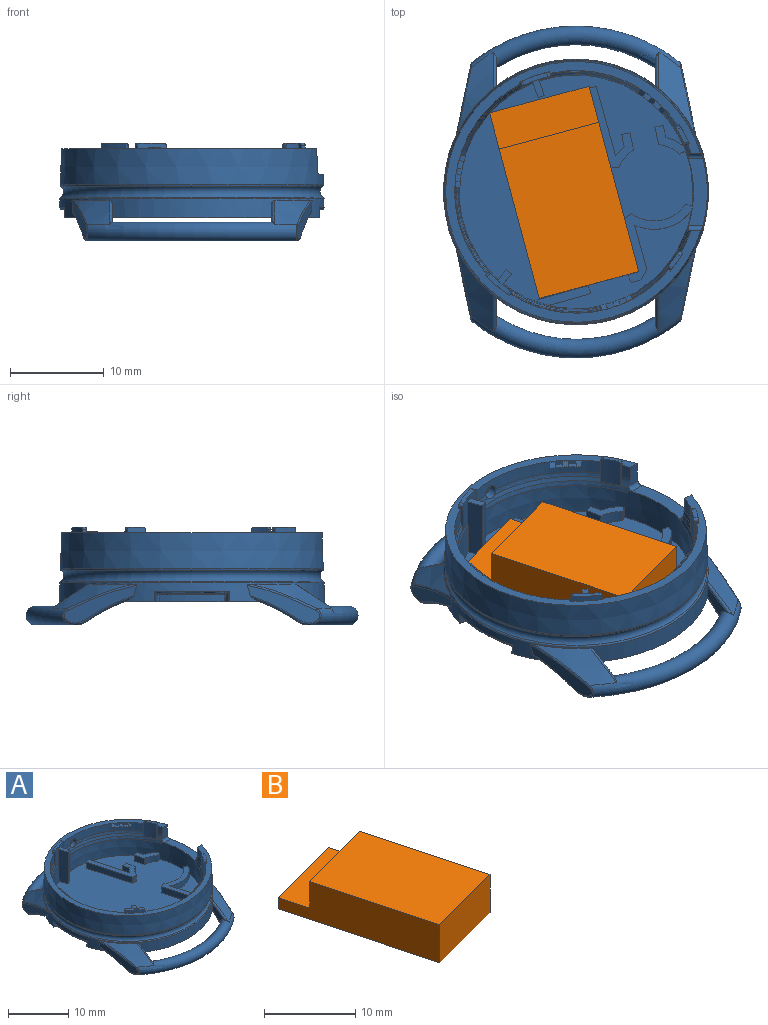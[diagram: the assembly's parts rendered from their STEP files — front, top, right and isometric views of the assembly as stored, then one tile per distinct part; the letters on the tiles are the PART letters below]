
ASSEMBLY  parts=2 mates=1
PART A: 217 faces, bbox 31.1x38.4x10.5 mm
  f0: plane 3.07x2.92mm, normal (-1,0,0), area 3.4mm2, adj f1,f17,f18,f28
  f1: cone r=14.15mm half-angle=2deg, axis (0,0,-1), area 109.4mm2, adj f0,f2,f4,f11,f12,f13,f15,f16
  f2: torus R=13.89mm, axis (0,0,-1), area 3.2mm2, adj f1,f3,f7,f10,f11,f216
  f3: plane 0.91x0.85mm, normal (0.28,0.96,0), area 0.7mm2, adj f2,f4,f6,f7,f216
  f4: plane 28.4x27.26mm, normal (0,0,-1), area 613.3mm2, adj f1,f3,f5,f6,f9,f10,f11,f12
  f5: cone r=13.08mm half-angle=5.2deg, axis (0,0,1), area 5mm2, adj f4,f6,f8,f9
  f6: cylinder r=0.15mm len=0.88mm, axis (0.09,-0.02,1), area 0.2mm2, adj f3,f4,f5,f7,f8
  f7: plane 7.66x1.15mm, normal (0,0,-1), area 4.8mm2, adj f2,f3,f6,f8,f9,f10
  f8: torus R=13.26mm, axis (0,0,-1), area 1.6mm2, adj f5,f6,f7,f9
  f9: cylinder r=0.15mm len=0.88mm, axis (-0.09,-0.02,-1), area 0.2mm2, adj f4,f5,f7,f8,f10
  f10: plane 0.91x0.85mm, normal (0.28,-0.96,0), area 0.7mm2, adj f2,f4,f7,f9,f11
  f11: cylinder r=0.1mm len=1.11mm, axis (-0.03,-0.01,1), area 0.2mm2, adj f1,f2,f4,f10
  f12: bspline ~5.59x2.9mm, area 3mm2, adj f1,f4,f13,f14,f29
  f13: plane 7.77x4.01mm, normal (0.98,0.19,-0.03), area 11mm2, adj f1,f12,f14,f15
  f14: bspline ~2.51x1.82mm, area 1.2mm2, adj f12,f13,f15,f18
  f15: bspline ~7.51x2.94mm, area 2mm2, adj f1,f13,f14,f16
  f16: cone r=15.73mm half-angle=51.5deg, axis (0,0,-1), area 19.2mm2, adj f1,f15,f17,f18
  f17: bspline ~4.16x2.88mm, area 2mm2, adj f0,f1,f16,f18
  f18: torus R=16.72mm, axis (0,0,1), area 134.1mm2, adj f0,f14,f16,f17,f19,f20,f21,f22
  f19: cone r=15.04mm half-angle=40.5deg, axis (0,0,-1), area 12.1mm2, adj f4,f18,f20,f24
  f20: bspline ~2.47x2.39mm, area 0.8mm2, adj f1,f4,f18,f19,f21
  f21: plane 3.07x2.92mm, normal (1,0,0), area 3.4mm2, adj f1,f18,f20,f22
  f22: bspline ~4.16x2.88mm, area 2mm2, adj f1,f18,f21,f27
  f23: bspline ~2.51x1.82mm, area 1.2mm2, adj f18,f24,f25,f26
  f24: bspline ~5.59x2.9mm, area 3mm2, adj f1,f4,f19,f23,f25
  f25: plane 7.76x4mm, normal (-0.98,0.19,-0.03), area 11mm2, adj f1,f23,f24,f26
  f26: bspline ~7.51x2.94mm, area 2mm2, adj f1,f23,f25,f27
  f27: cone r=15.73mm half-angle=51.5deg, axis (0,0,-1), area 19.2mm2, adj f1,f18,f22,f26
  f28: bspline ~2.47x2.39mm, area 0.8mm2, adj f0,f1,f4,f18,f29
  f29: cone r=15.04mm half-angle=40.5deg, axis (0,0,-1), area 12.1mm2, adj f4,f12,f18,f28
  f30: cylinder r=0.1mm len=1.11mm, axis (-0.03,0.01,-1), area 0.2mm2, adj f1,f4,f31,f32
  f31: torus R=13.89mm, axis (0,0,-1), area 3.2mm2, adj f1,f30,f32,f33,f38,f39
  f32: plane 0.91x0.85mm, normal (-0.28,-0.96,0), area 0.7mm2, adj f4,f30,f31,f33,f35
  f33: plane 7.66x1.15mm, normal (0,0,-1), area 4.8mm2, adj f31,f32,f34,f35,f37,f38
  f34: torus R=13.26mm, axis (0,0,-1), area 1.6mm2, adj f33,f35,f36,f37
  f35: cylinder r=0.15mm len=0.88mm, axis (0.09,-0.02,-1), area 0.2mm2, adj f4,f32,f33,f34,f36
  f36: cone r=13.08mm half-angle=5.2deg, axis (0,0,1), area 5mm2, adj f4,f34,f35,f37
  f37: cylinder r=0.15mm len=0.88mm, axis (-0.09,-0.02,1), area 0.2mm2, adj f4,f33,f34,f36,f38
  f38: plane 0.91x0.85mm, normal (-0.28,0.96,0), area 0.7mm2, adj f4,f31,f33,f37,f39
  f39: cylinder r=0.1mm len=1.11mm, axis (0.03,0.01,1), area 0.2mm2, adj f1,f4,f31,f38
  f40: bspline ~5.59x2.9mm, area 3mm2, adj f1,f4,f41,f46,f58
  f41: cone r=15.04mm half-angle=40.5deg, axis (0,0,-1), area 12.1mm2, adj f4,f40,f42,f45
  f42: bspline ~2.47x2.39mm, area 0.8mm2, adj f1,f4,f41,f43,f45
  f43: plane 3.07x2.92mm, normal (-1,0,0), area 3.4mm2, adj f1,f42,f44,f45
  f44: bspline ~4.16x2.88mm, area 2mm2, adj f1,f43,f45,f57
  f45: torus R=16.72mm, axis (0,0,1), area 134.1mm2, adj f41,f42,f43,f44,f46,f47,f51,f52
  f46: bspline ~2.51x1.82mm, area 1.2mm2, adj f40,f45,f56,f58
  f47: bspline ~2.51x1.82mm, area 1.2mm2, adj f45,f48,f49,f50
  f48: bspline ~5.59x2.9mm, area 3mm2, adj f1,f4,f47,f49,f55
  f49: plane 7.76x4mm, normal (-0.98,-0.19,-0.03), area 11mm2, adj f1,f47,f48,f50
  f50: bspline ~7.51x2.94mm, area 2mm2, adj f1,f47,f49,f51
  f51: cone r=15.73mm half-angle=51.5deg, axis (0,0,-1), area 19.2mm2, adj f1,f45,f50,f52
  f52: bspline ~4.16x2.88mm, area 2mm2, adj f1,f45,f51,f53
  f53: plane 3.07x2.92mm, normal (1,0,0), area 3.4mm2, adj f1,f45,f52,f54
  f54: bspline ~2.47x2.39mm, area 0.8mm2, adj f1,f4,f45,f53,f55
  f55: cone r=15.04mm half-angle=40.5deg, axis (0,0,-1), area 12.1mm2, adj f4,f45,f48,f54
  f56: bspline ~7.51x2.94mm, area 2mm2, adj f1,f46,f57,f58
  f57: cone r=15.73mm half-angle=51.5deg, axis (0,0,-1), area 19.2mm2, adj f1,f44,f45,f56
  f58: plane 7.77x4.01mm, normal (0.98,-0.19,-0.03), area 11mm2, adj f1,f40,f46,f56
  f59: torus R=13.86mm, axis (0,0,-1), area 21.4mm2, adj f1,f60
  f60: torus R=14.36mm, axis (0,0,-1), area 113.2mm2, adj f59,f61
  f61: torus R=13.81mm, axis (0,0,1), area 21.3mm2, adj f60,f62
  f62: cone r=13.99mm half-angle=2deg, axis (0,0,-1), area 312.4mm2, adj f61,f63,f94,f120,f121,f122,f177,f185
  f63: bspline ~1.82x1.79mm, area 1mm2, adj f62,f64,f177
  f64: cylinder r=0.75mm len=1.5mm, axis (0,1,0), area 4mm2, adj f63,f65,f69,f97,f124,f177
  f65: cone r=12.72mm half-angle=17.9deg, axis (0,0,1), area 7.6mm2, adj f64,f69,f71,f89,f97,f176
  f66: cone r=12.72mm half-angle=17.9deg, axis (0,0,1), area 11.7mm2, adj f87,f95,f96,f100,f104,f214
  f67: cone r=12.72mm half-angle=17.9deg, axis (0,0,1), area 10.5mm2, adj f88,f98,f99,f104,f105,f121,f122,f178
  f68: cone r=12.72mm half-angle=17.9deg, axis (0,0,1), area 0.5mm2, adj f70,f89,f93,f185,f186
  f69: torus R=10.9mm, axis (0,0,1), area 6.5mm2, adj f64,f65,f71,f124
  f70: torus R=10.9mm, axis (0,0,1), area 0.5mm2, adj f68,f93,f127,f185
  f71: plane 2.91x0.48mm, normal (-0.54,0.84,0.02), area 0.8mm2, adj f65,f69,f72,f73,f75,f90,f94,f124
  f72: cylinder r=0.3mm len=0.57mm, axis (-0.84,-0.54,0), area 0.2mm2, adj f71,f73,f75,f79
  f73: cone r=12.63mm half-angle=1deg, axis (0,0,1), area 7.1mm2, adj f71,f72,f74,f79,f90,f93
  f74: cylinder r=0.3mm len=0.56mm, axis (0.92,0.39,0), area 0.2mm2, adj f73,f75,f79,f93
  f75: cone r=13.14mm half-angle=2deg, axis (0,0,-1), area 1.3mm2, adj f71,f72,f74,f79,f93,f94
  f76: plane 2.75x1.38mm, normal (0,0,1), area 1.3mm2, adj f80,f81,f82,f83
  f77: plane 2.42x2.14mm, normal (0,0,1), area 1.3mm2, adj f101,f102,f103,f104
  f78: plane 1.62x1.33mm, normal (0,0,1), area 0.8mm2, adj f179,f180,f181,f182
  f79: plane 1.67x1.18mm, normal (0,0,1), area 0.8mm2, adj f72,f73,f74,f75
  f80: cylinder r=0.3mm len=0.54mm, axis (-0.22,0.98,0), area 0.2mm2, adj f76,f81,f83,f176
  f81: cone r=13.14mm half-angle=2deg, axis (0,0,-1), area 2mm2, adj f76,f80,f82,f94,f95,f176
  f82: cylinder r=0.3mm len=0.57mm, axis (0.46,-0.89,0), area 0.2mm2, adj f76,f81,f83,f95
  f83: cone r=12.63mm half-angle=1deg, axis (0,0,1), area 8.7mm2, adj f76,f80,f82,f84,f86,f91,f92,f95
  f84: plane 1.94x1.28mm, normal (0,0,1), area 1.3mm2, adj f83,f86,f212,f213
  f85: plane 1.59x1.5mm, normal (0,0,1), area 1mm2, adj f104,f105,f214,f215
  f86: plane 6.5x1.72mm, normal (0.94,0.34,0), area 11.2mm2, adj f83,f84,f89,f106,f117,f213
  f87: torus R=14.55mm, axis (0,0,1), area 15.2mm2, adj f66,f92,f118,f212,f214
  f88: torus R=14.55mm, axis (0,0,1), area 14.3mm2, adj f67,f105,f117,f120,f121,f187
  f89: torus R=14.55mm, axis (0,0,1), area 11.7mm2, adj f65,f68,f86,f90,f91,f117,f119,f120
  f90: cone r=12.62mm half-angle=17.9deg, axis (0,0,1), area 0.3mm2, adj f71,f73,f89,f93
  f91: cone r=12.62mm half-angle=17.9deg, axis (0,0,1), area 0.2mm2, adj f83,f89,f176
  f92: cone r=12.62mm half-angle=17.9deg, axis (0,0,1), area 0.2mm2, adj f83,f87,f95
  f93: plane 2.91x0.48mm, normal (0.39,-0.92,0.02), area 0.8mm2, adj f68,f70,f73,f74,f75,f90,f94,f127
  f94: plane 27.85x27.24mm, normal (0,0,1), area 71.4mm2, adj f62,f71,f75,f81,f93,f95,f100,f102
  f95: plane 2.91x0.51mm, normal (-0.89,-0.46,0.02), area 0.8mm2, adj f66,f81,f82,f83,f92,f94,f96,f123
  f96: torus R=10.9mm, axis (0,0,1), area 12.7mm2, adj f66,f95,f100,f123
  f97: torus R=10.9mm, axis (0,0,1), area 1.2mm2, adj f64,f65,f124,f176
  f98: torus R=10.9mm, axis (0,0,1), area 10mm2, adj f67,f126,f183,f184
  f99: torus R=10.9mm, axis (0,0,1), area 1.4mm2, adj f67,f122,f125,f178
  f100: plane 2.77x0.37mm, normal (-0.68,0.74,0.02), area 0.7mm2, adj f66,f94,f96,f101,f102,f104,f123
  f101: cylinder r=0.3mm len=0.57mm, axis (-0.74,-0.68,0), area 0.2mm2, adj f77,f100,f102,f104
  f102: cone r=13.14mm half-angle=2deg, axis (0,0,-1), area 2mm2, adj f77,f94,f100,f101,f103,f184
  f103: cylinder r=0.3mm len=0.58mm, axis (0.54,0.84,0), area 0.2mm2, adj f77,f102,f104,f184
  f104: cylinder r=12.65mm len=3.07mm, axis (0,0,1), area 8.3mm2, adj f66,f67,f77,f85,f100,f101,f103,f105
  f105: plane 6.49x1.15mm, normal (0.77,-0.64,0), area 9.2mm2, adj f67,f85,f88,f104,f106,f117,f215
  f106: plane 24.98x24.98mm, normal (0,0,1), area 455.3mm2, adj f86,f105,f107,f108,f109,f110,f111,f112
  f107: plane 1.25x0.95mm, normal (-0.05,-1,0), area 1.2mm2, adj f106,f108,f115,f116
  f108: plane 8.38x2.32mm, normal (-0.96,-0.27,0), area 10.9mm2, adj f106,f107,f109,f116
  f109: plane 1.25x0.87mm, normal (-0.27,0.96,0), area 1.1mm2, adj f106,f108,f110,f116
  f110: plane 7.44x2.05mm, normal (0.96,0.27,0), area 9.6mm2, adj f106,f109,f111,f116
  f111: cylinder r=5mm len=1.25mm, axis (0,0,1), area 1.7mm2, adj f106,f110,f112,f116
  f112: plane 1.27x1.25mm, normal (-0.98,-0.22,0), area 1.6mm2, adj f106,f111,f113,f116
  f113: plane 1.25x0.88mm, normal (-0.22,0.98,0), area 1.1mm2, adj f106,f112,f114,f116
  f114: plane 1.84x1.25mm, normal (0.98,0.22,0), area 2.4mm2, adj f106,f113,f115,f116
  f115: cylinder r=4.1mm len=1.85mm, axis (0,0,1), area 3.1mm2, adj f106,f107,f114,f116
  f116: plane 8.67x4.85mm, normal (0,0,1), area 11.1mm2, adj f107,f108,f109,f110,f111,f112,f113,f114
  f117: cone r=12.52mm half-angle=1deg, axis (0,0,1), area 171mm2, adj f86,f88,f89,f105,f106,f119,f120,f187
  f118: cone r=12.52mm half-angle=1deg, axis (0,0,1), area 83.7mm2, adj f87,f106,f212,f214
  f119: plane 0.32x0.04mm, normal (0,1,0), area 0mm2, adj f89,f117,f120
  f120: plane 8.15x2.15mm, normal (0,0,1), area 10.7mm2, adj f62,f88,f89,f117,f119,f121,f186,f187
  f121: cylinder r=0.5mm len=1.57mm, axis (1,0,0), area 1.1mm2, adj f62,f67,f88,f120,f122
  f122: plane 2.26x1.36mm, normal (0,1,0), area 2.5mm2, adj f62,f67,f94,f99,f121,f125
  f123: cone r=12.93mm half-angle=2.5deg, axis (0,0,1), area 31.8mm2, adj f94,f95,f96,f100,f128,f129,f130,f132
  f124: cone r=12.93mm half-angle=2.5deg, axis (0,0,1), area 19.1mm2, adj f64,f69,f71,f94,f97,f160,f161,f162
  f125: cone r=12.93mm half-angle=2.5deg, axis (0,0,1), area 3.9mm2, adj f94,f99,f122,f178
  f126: cone r=12.93mm half-angle=2.5deg, axis (0,0,1), area 24.3mm2, adj f94,f98,f144,f145,f146,f148,f149,f150
  f127: cone r=12.93mm half-angle=2.5deg, axis (0,0,1), area 1.5mm2, adj f70,f93,f94,f185
  f128: plane 0.59x0.22mm, normal (0,0,1), area 0mm2, adj f123,f131,f132,f139
  f129: plane 0.6x0.16mm, normal (0,0,1), area 0mm2, adj f123,f141,f142,f143
  f130: plane 0.61x0.09mm, normal (0,0,1), area 0mm2, adj f123,f134,f135,f136
  f131: cone r=12.65mm half-angle=51.3deg, axis (0,0,1), area 0.4mm2, adj f128,f132,f139,f140
  f132: plane 1.1x0.55mm, normal (0.17,0.98,0), area 0.5mm2, adj f123,f128,f131,f133,f140
  f133: plane 3.46x1.1mm, normal (0,0,-1), area 1.7mm2, adj f123,f132,f134,f140
  f134: plane 1.1x0.55mm, normal (-0.17,-0.98,0), area 0.5mm2, adj f123,f130,f133,f135,f140
  f135: cone r=12.65mm half-angle=51.3deg, axis (0,0,1), area 0.4mm2, adj f130,f134,f136,f140
  f136: plane 0.55x0.4mm, normal (0.17,0.98,0), area 0.1mm2, adj f123,f130,f135,f138
  f137: plane 0.91x0.72mm, normal (0,0,1), area 0.5mm2, adj f123,f139,f140,f142
  f138: plane 0.88x0.62mm, normal (0,0,1), area 0.4mm2, adj f123,f136,f140,f143
  f139: plane 0.55x0.4mm, normal (-0.17,-0.98,0), area 0.1mm2, adj f123,f128,f131,f137
  f140: cylinder r=12.4mm len=3.38mm, axis (0,0,-1), area 2.4mm2, adj f131,f132,f133,f134,f135,f137,f138,f141
  f141: cone r=12.65mm half-angle=51.3deg, axis (0,0,1), area 0.4mm2, adj f129,f140,f142,f143
  f142: plane 0.55x0.4mm, normal (0.17,0.98,0), area 0.1mm2, adj f123,f129,f137,f141
  f143: plane 0.55x0.4mm, normal (-0.17,-0.98,0), area 0.1mm2, adj f123,f129,f138,f141
  f144: plane 0.61x0.19mm, normal (0,0,1), area 0mm2, adj f126,f147,f148,f155
  f145: plane 0.58x0.26mm, normal (0,0,1), area 0mm2, adj f126,f157,f158,f159
  f146: plane 0.56x0.32mm, normal (0,0,1), area 0mm2, adj f126,f150,f151,f152
  f147: cone r=12.65mm half-angle=51.3deg, axis (0,0,1), area 0.4mm2, adj f144,f148,f155,f156
  f148: plane 1.1x0.53mm, normal (-0.94,-0.34,0), area 0.5mm2, adj f126,f144,f147,f149,f156
  f149: plane 3.4x1.65mm, normal (0,0,-1), area 1.7mm2, adj f126,f148,f150,f156
  f150: plane 1.1x0.53mm, normal (0.94,0.34,0), area 0.5mm2, adj f126,f146,f149,f151,f156
  f151: cone r=12.65mm half-angle=51.3deg, axis (0,0,1), area 0.4mm2, adj f146,f150,f152,f156
  f152: plane 0.52x0.4mm, normal (-0.94,-0.34,0), area 0.1mm2, adj f126,f146,f151,f154
  f153: plane 0.99x0.75mm, normal (0,0,1), area 0.5mm2, adj f126,f155,f156,f158
  f154: plane 0.91x0.82mm, normal (0,0,1), area 0.4mm2, adj f126,f152,f156,f159
  f155: plane 0.52x0.4mm, normal (0.94,0.34,0), area 0.1mm2, adj f126,f144,f147,f153
  f156: cylinder r=12.4mm len=3.22mm, axis (0,0,-1), area 2.4mm2, adj f147,f148,f149,f150,f151,f153,f154,f157
  f157: cone r=12.65mm half-angle=51.3deg, axis (0,0,1), area 0.4mm2, adj f145,f156,f158,f159
  f158: plane 0.52x0.4mm, normal (-0.94,-0.34,0), area 0.1mm2, adj f126,f145,f153,f157
  f159: plane 0.52x0.4mm, normal (0.94,0.34,0), area 0.1mm2, adj f126,f145,f154,f157
  f160: plane 0.48x0.45mm, normal (0,0,1), area 0mm2, adj f124,f163,f164,f171
  f161: plane 0.5x0.43mm, normal (0,0,1), area 0mm2, adj f124,f173,f174,f175
  f162: plane 0.54x0.38mm, normal (0,0,1), area 0mm2, adj f124,f166,f167,f168
  f163: cone r=12.65mm half-angle=51.3deg, axis (0,0,1), area 0.4mm2, adj f160,f164,f171,f172
  f164: plane 1.1x0.43mm, normal (0.77,-0.64,0), area 0.5mm2, adj f124,f160,f163,f165,f172
  f165: plane 2.95x2.59mm, normal (0,0,-1), area 1.7mm2, adj f124,f164,f166,f172
  f166: plane 1.1x0.43mm, normal (-0.77,0.64,0), area 0.5mm2, adj f124,f162,f165,f167,f172
  f167: cone r=12.65mm half-angle=51.3deg, axis (0,0,1), area 0.4mm2, adj f162,f166,f168,f172
  f168: plane 0.43x0.4mm, normal (0.77,-0.64,0), area 0.1mm2, adj f124,f162,f167,f170
  f169: plane 0.99x0.96mm, normal (0,0,1), area 0.5mm2, adj f124,f171,f172,f174
  f170: plane 0.98x0.88mm, normal (0,0,1), area 0.4mm2, adj f124,f168,f172,f175
  f171: plane 0.43x0.4mm, normal (-0.77,0.64,0), area 0.1mm2, adj f124,f160,f163,f169
  f172: cylinder r=12.4mm len=2.63mm, axis (0,0,-1), area 2.4mm2, adj f163,f164,f165,f166,f167,f169,f170,f173
  f173: cone r=12.65mm half-angle=51.3deg, axis (0,0,1), area 0.4mm2, adj f161,f172,f174,f175
  f174: plane 0.42x0.4mm, normal (0.77,-0.64,0), area 0.1mm2, adj f124,f161,f169,f173
  f175: plane 0.42x0.4mm, normal (-0.77,0.64,0), area 0.1mm2, adj f124,f161,f170,f173
  f176: plane 2.91x0.52mm, normal (0.98,0.22,0.02), area 0.8mm2, adj f65,f80,f81,f83,f91,f94,f97,f124
  f177: bspline ~1.82x1.79mm, area -0.6mm2, adj f62,f63,f64
  f178: plane 2.77x0.44mm, normal (0.5,0.87,0.02), area 0.7mm2, adj f67,f94,f99,f125,f179,f180,f182
  f179: cylinder r=0.3mm len=0.58mm, axis (-0.87,0.5,0), area 0.2mm2, adj f78,f178,f180,f182
  f180: cylinder r=12.65mm len=3.07mm, axis (0,0,1), area 6.8mm2, adj f67,f78,f178,f179,f181,f183
  f181: cylinder r=0.3mm len=0.57mm, axis (0.77,-0.64,0), area 0.2mm2, adj f78,f180,f182,f183
  f182: cone r=13.14mm half-angle=2deg, axis (0,0,-1), area 1.3mm2, adj f78,f94,f178,f179,f181,f183
  f183: plane 2.77x0.41mm, normal (-0.64,-0.77,0.02), area 0.7mm2, adj f67,f94,f98,f126,f180,f181,f182
  f184: plane 2.77x0.42mm, normal (0.84,-0.54,0.02), area 0.7mm2, adj f67,f94,f98,f102,f103,f104,f126
  f185: plane 2.26x1.36mm, normal (0,-1,0), area 2.5mm2, adj f62,f68,f70,f94,f127,f186
  f186: cylinder r=0.5mm len=1.57mm, axis (-1,0,0), area 1.1mm2, adj f62,f68,f89,f120,f185
  f187: plane 0.32x0.04mm, normal (0,-1,0), area 0mm2, adj f88,f117,f120
  f188: cylinder r=12.49mm len=1.25mm, axis (0,0,1), area 1.4mm2, adj f117,f189,f194,f196
  f189: plane 1.25x0.3mm, normal (-0.96,-0.27,0), area 0.4mm2, adj f106,f188,f190,f196
  f190: plane 5.43x1.5mm, normal (-0.27,0.96,0), area 7mm2, adj f106,f189,f192,f196
  f191: plane 1.25x1.13mm, normal (-0.27,0.96,0), area 1.5mm2, adj f106,f195,f197,f198
  f192: plane 1.25x0.85mm, normal (0.94,0.34,0), area 1.1mm2, adj f106,f190,f194,f196
  f193: plane 1.25x1.07mm, normal (0.27,-0.96,0), area 1.4mm2, adj f106,f195,f197,f204
  f194: plane 4.59x1.27mm, normal (0.27,-0.96,0), area 5.9mm2, adj f106,f188,f192,f196
  f195: plane 1.25x0.85mm, normal (-0.94,-0.34,0), area 1.1mm2, adj f106,f191,f193,f197
  f196: plane 5.74x2.11mm, normal (0,0,1), area 4.8mm2, adj f188,f189,f190,f192,f194
  f197: plane 8.37x7.28mm, normal (0,0,1), area 13mm2, adj f117,f191,f193,f195,f198,f199,f200,f201
  f198: plane 5.67x1.56mm, normal (-0.96,-0.27,0), area 7.3mm2, adj f106,f191,f197,f199
  f199: plane 1.25x0.79mm, normal (-0.56,0.83,0), area 1.2mm2, adj f106,f197,f198,f200
  f200: cylinder r=4.1mm len=5.79mm, axis (0,0,1), area 8.2mm2, adj f106,f197,f199,f201
  f201: plane 1.25x0.71mm, normal (0.24,0.97,0), area 0.9mm2, adj f106,f117,f197,f200
  f202: cylinder r=5mm len=6.09mm, axis (0,0,1), area 8.5mm2, adj f106,f117,f197,f203
  f203: plane 4.72x1.3mm, normal (0.96,0.27,0), area 6.1mm2, adj f106,f197,f202,f204
  f204: plane 1.25x1.11mm, normal (0.87,-0.49,0), area 1.6mm2, adj f106,f193,f197,f203
  f205: plane 1.25x0.65mm, normal (0.46,-0.89,0), area 0.9mm2, adj f106,f117,f206,f207
  f206: plane 3.29x3.06mm, normal (0,0,1), area 3.7mm2, adj f117,f205,f207,f208,f209,f210,f211
  f207: cylinder r=4.1mm len=2.24mm, axis (0,0,1), area 3.1mm2, adj f106,f205,f206,f208
  f208: plane 1.84x1.25mm, normal (-0.98,-0.22,0), area 2.4mm2, adj f106,f206,f207,f209
  f209: plane 1.25x0.88mm, normal (-0.22,0.98,0), area 1.1mm2, adj f106,f206,f208,f210
  f210: plane 1.27x1.25mm, normal (0.98,0.22,0), area 1.6mm2, adj f106,f206,f209,f211
  f211: cylinder r=5mm len=1.95mm, axis (0,0,1), area 2.7mm2, adj f106,f117,f206,f210
  f212: plane 6.5x1.72mm, normal (-0.94,-0.34,0), area 11.2mm2, adj f83,f84,f87,f106,f118,f213
  f213: plane 6.49x0.66mm, normal (0.34,-0.94,0), area 4.5mm2, adj f84,f86,f106,f212
  f214: plane 6.49x1.15mm, normal (-0.77,0.64,0), area 9.2mm2, adj f66,f85,f87,f104,f106,f118,f215
  f215: plane 6.49x0.54mm, normal (0.64,0.77,0), area 4.5mm2, adj f85,f105,f106,f214
  f216: cylinder r=0.1mm len=1.11mm, axis (0.03,-0.01,-1), area 0.2mm2, adj f1,f2,f3,f4
PART B: 8 faces, bbox 15.9x22.6x5.1 mm
  f0: plane 19.8x5.31mm, normal (0.97,0.26,0), area 90.1mm2, adj f1,f3,f4,f5,f6,f7
  f1: plane 10.63x3.6mm, normal (-0.26,0.97,0), area 39.6mm2, adj f0,f2,f4,f7
  f2: plane 19.8x5.31mm, normal (-0.97,-0.26,0), area 90.1mm2, adj f1,f3,f4,f5,f6,f7
  f3: plane 10.63x5.1mm, normal (0.26,-0.97,0), area 56.1mm2, adj f0,f2,f4,f5
  f4: plane 18.78x14.9mm, normal (0,0,1), area 181.5mm2, adj f0,f1,f2,f3
  f5: plane 22.65x15.93mm, normal (0,0,-1), area 225.5mm2, adj f0,f2,f3,f6
  f6: plane 10.63x2.85mm, normal (-0.26,0.97,0), area 16.5mm2, adj f0,f2,f5,f7
  f7: plane 11.66x6.71mm, normal (0,0,1), area 44mm2, adj f0,f1,f2,f6
PLACE A t=(-23.95,-1.41,7.74)mm
PLACE B t=(-17.24,-9.92,7.74)mm
MATE revolute A.f106 <-> B.f5  axis (0,0,1) through (-17.24,-9.92,7.74)mm
